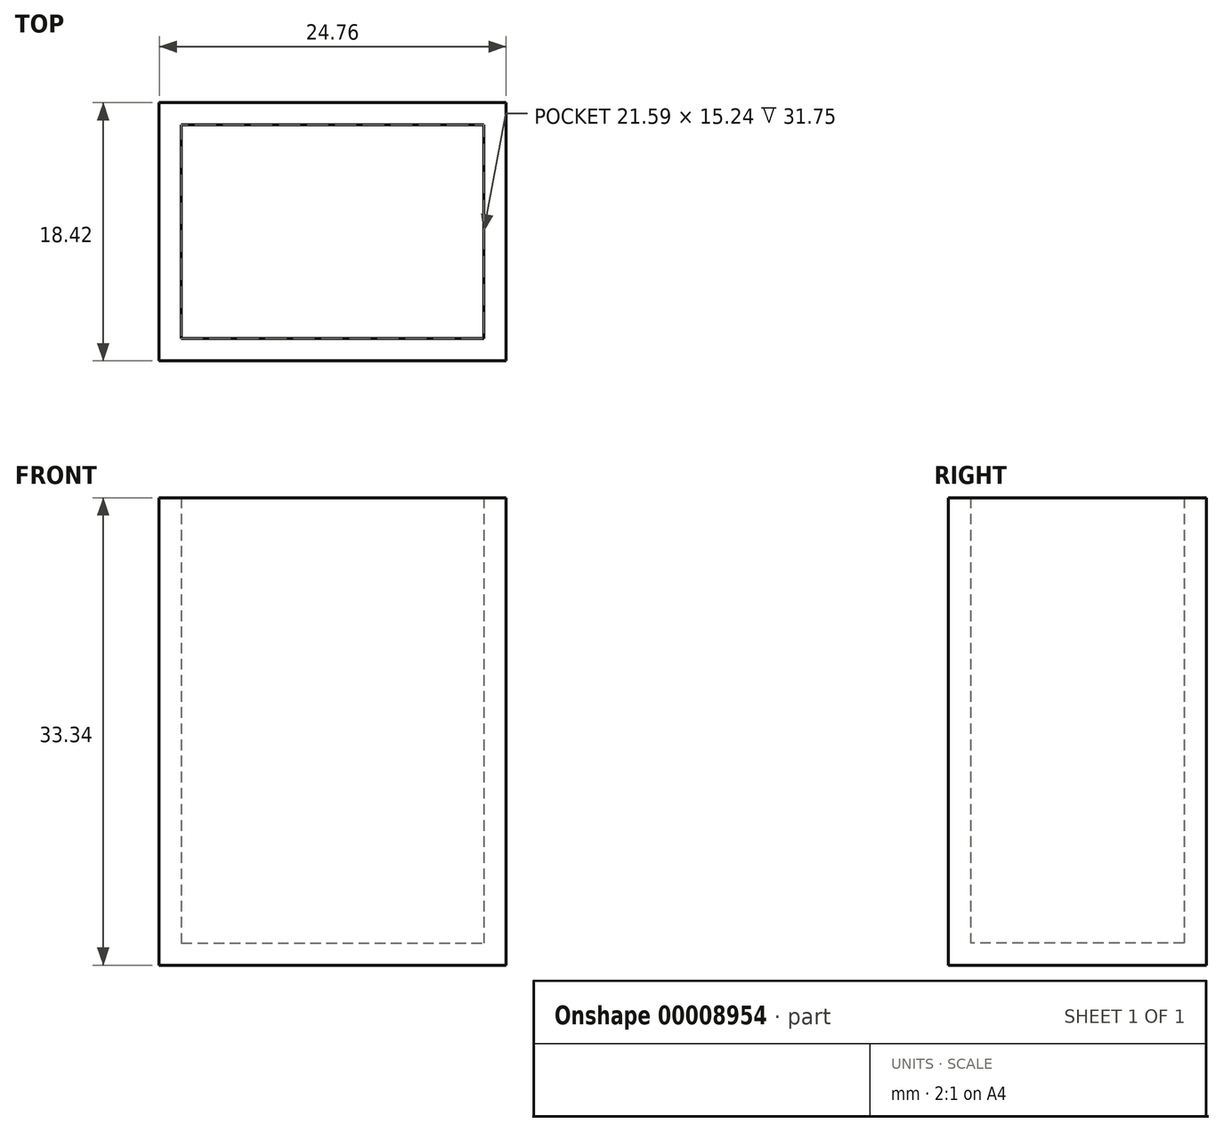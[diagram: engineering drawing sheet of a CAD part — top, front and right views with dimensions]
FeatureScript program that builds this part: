
annotation { "Feature Type Name" : "Feature", "Feature Type Description" : "" }
export const myFeature = defineFeature(function(context is Context, id is Id, definition is map)
    precondition{}
    {
        {
            var Q0;
            Q0=qCreatedBy(makeId("Top.planeOp"),FACE);
            var sketch = newSketch(context, id + "F0", { "sketchPlane" : qUnion([Q0])});
            skLineSegment(sketch, "E0.bottom", {"start": v(-11.11, 7.94) * mm, "end": v(11.11, 7.94) * mm});
            skLineSegment(sketch, "E0.top", {"start": v(-11.11, -7.94) * mm, "end": v(11.11, -7.94) * mm});
            skLineSegment(sketch, "E0.left", {"start": v(-11.11, 7.94) * mm, "end": v(-11.11, -7.94) * mm});
            skLineSegment(sketch, "E0.right", {"start": v(11.11, 7.94) * mm, "end": v(11.11, -7.94) * mm});
            skLineSegment(sketch, "E1.0", {"start": v(-12.38, 9.2) * mm, "end": v(12.38, 9.2) * mm});
            skLineSegment(sketch, "E1.1", {"start": v(-12.38, 9.2) * mm, "end": v(-12.38, -9.2) * mm});
            skLineSegment(sketch, "E1.2", {"start": v(-12.38, -9.2) * mm, "end": v(12.38, -9.2) * mm});
            skLineSegment(sketch, "E1.3", {"start": v(12.38, 9.2) * mm, "end": v(12.38, -9.2) * mm});
            skSolve(sketch);
        }
        {
            var Q0;
            Q0=makeQuery(id+"F0.imprint","IMPRINT",FACE,{"disambiguationData":[TD([[makeQuery(id+"F0.imprint","IMPRINT",EDGE,{"derivedFrom":sQuery(id+"F0.wireOp",EDGE,"E0.bottom")}),1.0]])]});
            var Q1;
            Q1=makeQuery(id+"F0.imprint","IMPRINT",FACE,{"disambiguationData":[TD([[makeQuery(id+"F0.imprint","IMPRINT",EDGE,{"derivedFrom":sQuery(id+"F0.wireOp",EDGE,"E0.bottom")}),-1.0]])]});
            extrude(context, id + "F1", {"entities" : qUnion([Q0, Q1]), "depth" : 1.59 * mm, "offsetDistance" : 25.4 * mm});
        }
        {
            var Q0;
            Q0=makeQuery(id+"F1.opExtrude","CAP_FACE",FACE,{"disambiguationData":[OSD([sQuery(id+"F0.wireOp",EDGE,"E1.0"),sQuery(id+"F0.wireOp",EDGE,"E1.1"),sQuery(id+"F0.wireOp",EDGE,"E1.2"),sQuery(id+"F0.wireOp",EDGE,"E1.3")])],"isStart":false});
            var sketch = newSketch(context, id + "F2", { "sketchPlane" : qUnion([Q0])});
            skLineSegment(sketch, "E2.0", {"start": v(-12.38, 9.2) * mm, "end": v(-12.38, -9.2) * mm});
            skLineSegment(sketch, "E3.0", {"start": v(-12.38, 9.2) * mm, "end": v(12.38, 9.2) * mm});
            skLineSegment(sketch, "E4.0", {"start": v(-12.38, -9.2) * mm, "end": v(12.38, -9.2) * mm});
            skLineSegment(sketch, "E5.0", {"start": v(12.38, 9.2) * mm, "end": v(12.38, -9.2) * mm});
            skLineSegment(sketch, "E6.0", {"start": v(-10.8, 7.62) * mm, "end": v(10.8, 7.62) * mm});
            skLineSegment(sketch, "E6.1", {"start": v(-10.8, 7.62) * mm, "end": v(-10.8, -7.62) * mm});
            skLineSegment(sketch, "E6.2", {"start": v(-10.8, -7.62) * mm, "end": v(10.8, -7.62) * mm});
            skLineSegment(sketch, "E6.3", {"start": v(10.8, 7.62) * mm, "end": v(10.8, -7.62) * mm});
            skSolve(sketch);
        }
        {
            var Q0;
            Q0=makeQuery(id+"F2.imprint","IMPRINT",FACE,{"disambiguationData":[TD([[makeQuery(id+"F2.imprint","IMPRINT",EDGE,{"derivedFrom":sQuery(id+"F2.wireOp",EDGE,"E2.0")}),1.0]])]});
            extrude(context, id + "F3", {"entities" : qUnion([Q0]), "operationType" : NewBodyOperationType.ADD, "depth" : 31.75 * mm, "offsetDistance" : 25.4 * mm});
        }
    });
